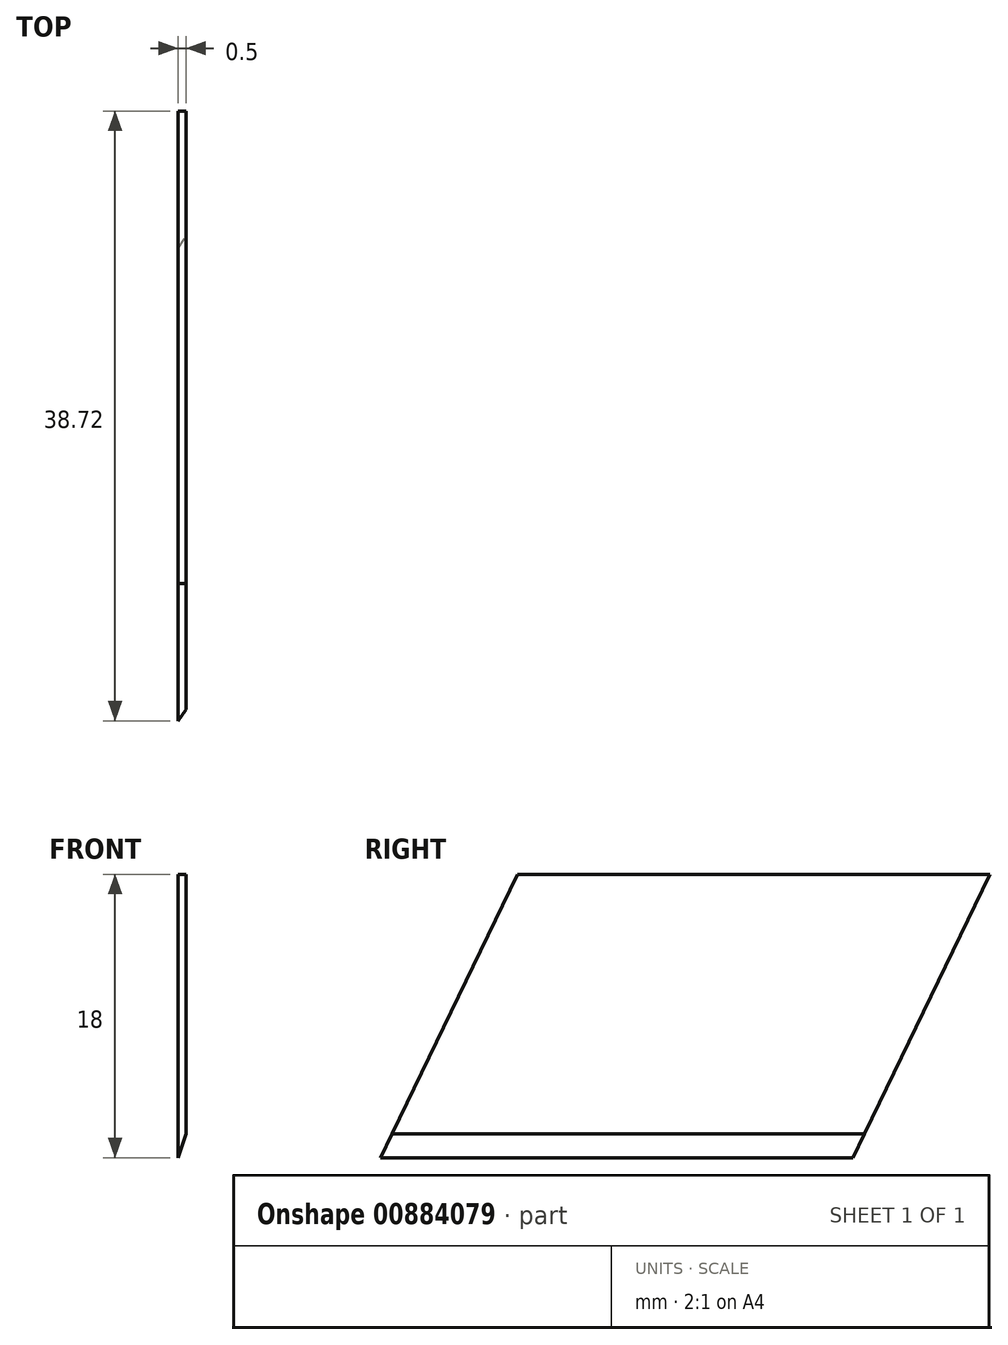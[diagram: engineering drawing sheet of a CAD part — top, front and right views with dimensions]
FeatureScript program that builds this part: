
annotation { "Feature Type Name" : "Feature", "Feature Type Description" : "" }
export const myFeature = defineFeature(function(context is Context, id is Id, definition is map)
    precondition{}
    {
        {
            var Q0;
            Q0=qCreatedBy(makeId("Right.planeOp"),FACE);
            var sketch = newSketch(context, id + "F0", { "sketchPlane" : qUnion([Q0])});
            skLineSegment(sketch, "E0", {"start": v(-15, 0) * mm, "end": v(15, 0) * mm});
            skLineSegment(sketch, "E1", {"start": v(15, 0) * mm, "end": v(6.28, -18) * mm});
            skLineSegment(sketch, "E2", {"start": v(6.28, -18) * mm, "end": v(-23.72, -18) * mm});
            skLineSegment(sketch, "E3", {"start": v(-23.72, -18) * mm, "end": v(-15, 0) * mm});
            skSolve(sketch);
        }
        {
            var Q0;
            Q0=makeQuery(id+"F0.imprint","IMPRINT",FACE,{"disambiguationData":[TD([[makeQuery(id+"F0.imprint","IMPRINT",EDGE,{"derivedFrom":sQuery(id+"F0.wireOp",EDGE,"E0")}),-1.0]])]});
            extrude(context, id + "F1", {"entities" : qUnion([Q0]), "depth" : .5 * mm, "offsetDistance" : 25 * mm});
        }
        {
            var Q0;
            Q0=makeQuery(id+"F1.opExtrude","CAP_EDGE",EDGE,{"disambiguationData":[OSD([sQuery(id+"F0.wireOp",EDGE,"E2")])],"isStart":false});
            chamfer(context, id + "F2", {"entities" : qUnion([Q0]), "chamferType" : ChamferType.TWO_OFFSETS, "width1" : .5 * mm, "oppositeDirection" : false, "width2" : 1.5 * mm, "tangentPropagation" : true});
        }
    });
